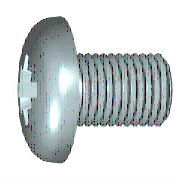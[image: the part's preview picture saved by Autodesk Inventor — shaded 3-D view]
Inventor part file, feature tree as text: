
AUTODESK INVENTOR PART (.ipt)
format: ipt  version: 2022 (Build 260153000, 153)  size: 337,408 bytes
history: native  units: mm (DEFAULTED — no unit token found)
features: other x2, plane x2, extrude x2
ambient origin geometry x7: Origin, YZ Plane, XZ Plane, X Axis, Y Axis, Z Axis, Center Point
bodies: Solid1 (feature_tree)
feature tree (6):
  other  "Базовый элемент"
  plane  "Work Plane1"
  extrude  "Паз"  Depth=8.0mm
  other  "Вырез"
  extrude  "Прорезь крестообразная"  Depth=4.39mm
  plane  "Work Plane3"
